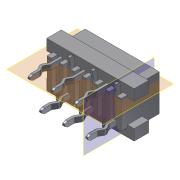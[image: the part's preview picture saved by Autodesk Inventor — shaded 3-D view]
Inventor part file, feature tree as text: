
AUTODESK INVENTOR PART (.ipt)
format: ipt  version: 2014 (Build 180170000, 170)  size: 701,952 bytes
history: native  units: mm
features: other x3, plane x2
ambient origin geometry x8: Origin, YZ Plane, XZ Plane, XY Plane, X Axis, Y Axis, Z Axis, Center Point
bodies: Volumenkörper1 (feature_tree)
feature tree (5):
  other  "micro-miniature_steckverbinder_a-32-06v-130x0"
  other  "Arbeitspunkt1"
  other  "Arbeitspunkt2"
  plane  "Arbeitsebene1"
  plane  "Arbeitsebene2"
